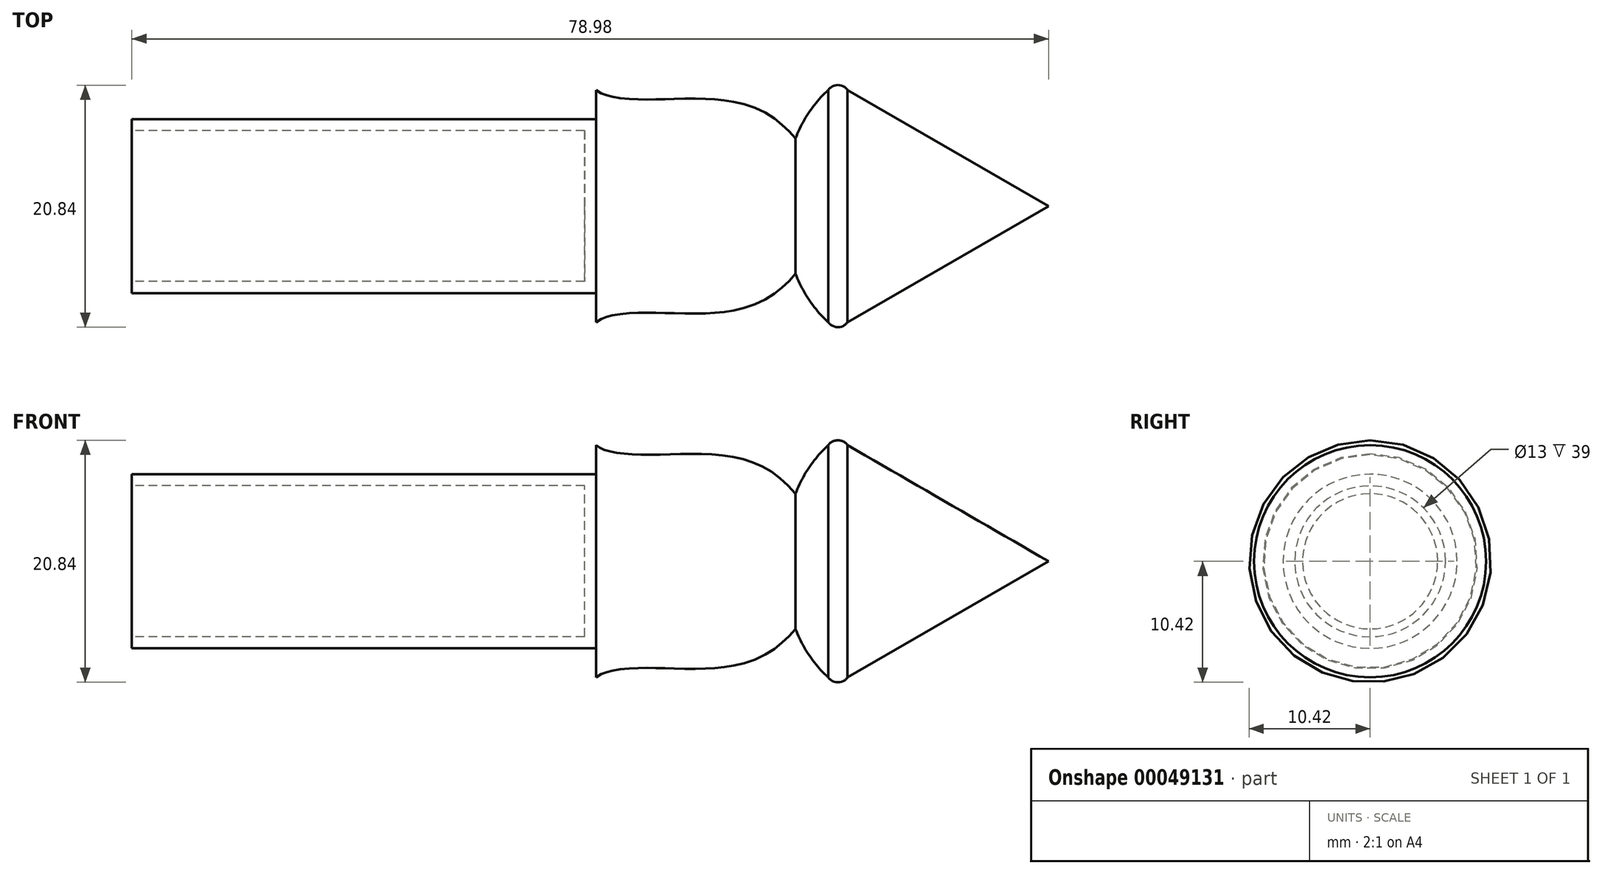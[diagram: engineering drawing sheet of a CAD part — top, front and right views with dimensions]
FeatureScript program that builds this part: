
annotation { "Feature Type Name" : "Feature", "Feature Type Description" : "" }
export const myFeature = defineFeature(function(context is Context, id is Id, definition is map)
    precondition{}
    {
        {
            var Q0;
            Q0=qCreatedBy(makeId("Top.planeOp"),FACE);
            var sketch = newSketch(context, id + "F0", { "sketchPlane" : qUnion([Q0])});
            skLineSegment(sketch, "E0.bottom", {"start": v(-43.36, 7.5) * mm, "end": v(-3.36, 7.5) * mm});
            skLineSegment(sketch, "E0.top", {"start": v(-43.36, 0) * mm, "end": v(-3.36, 0) * mm});
            skLineSegment(sketch, "E0.left", {"start": v(-43.36, 7.5) * mm, "end": v(-43.36, 0) * mm});
            skLineSegment(sketch, "E0.right", {"start": v(-3.36, 7.5) * mm, "end": v(-3.36, 0) * mm});
            skLineSegment(sketch, "E1", {"start": v(-3.36, 7.5) * mm, "end": v(-3.36, 10) * mm});
            skFitSpline(sketch, "E2", {"points": [v(-3.36, 10) * mm, v(1.33, 9.18) * mm, v(11.64, 7.79) * mm, v(16.64, 0) * mm], "startDerivative": vector(7.94, -7.27) * mm, "endDerivative": vector(1.37, -16.17) * mm});
            skLineSegment(sketch, "E3", {"start": v(-3.36, 0) * mm, "end": v(16.64, 0) * mm});
            skArc(sketch, "E4", {"start": v(16.64, 10) * mm, "mid": v(14.98, 8.08) * mm, "end": v(13.82, 5.82) * mm});
            skArc(sketch, "E5", {"start": v(18.3, 10) * mm, "mid": v(17.47, 10.42) * mm, "end": v(16.64, 10) * mm});
            skLineSegment(sketch, "E6", {"start": v(18.3, 10) * mm, "end": v(35.62, 0) * mm});
            skLineSegment(sketch, "E7", {"start": v(35.62, 0) * mm, "end": v(16.64, 0) * mm});
            skSolve(sketch);
        }
        {
            var Q0;
            Q0=makeQuery(id+"F0.imprint","IMPRINT",FACE,{"disambiguationData":[TD([[makeQuery(id+"F0.imprint","IMPRINT",EDGE,{"derivedFrom":sQuery(id+"F0.wireOp",EDGE,"E0.bottom")}),-1.0]])]});
            var Q1;
            Q1=sQuery(id+"F0.wireOp",EDGE,"E0.top");
            revolve(context, id + "F1", {"entities" : qUnion([Q0]), "axis" : qUnion([Q1]), "revolveType" : RevolveType.FULL});
        }
        {
            var Q0;
            Q0=makeQuery(id+"F1.opRevolve","SWEPT_FACE",FACE,{"disambiguationData":[OSD([sQuery(id+"F0.wireOp",EDGE,"E0.left")])]});
            shell(context, id + "F2", {"entities" : qUnion([Q0]), "thickness" : 1 * mm});
        }
        {
            var Q0;
            Q0=makeQuery(id+"F0.imprint","IMPRINT",FACE,{"disambiguationData":[TD([[makeQuery(id+"F0.imprint","IMPRINT",EDGE,{"derivedFrom":sQuery(id+"F0.wireOp",EDGE,"E0.right")}),1.0]])]});
            var Q1;
            {var subQ2=sQuery(id+"F0.wireOp",EDGE,"E4");Q1=makeQuery(id+"F0.imprint","IMPRINT",FACE,{"disambiguationData":[TD([[makeQuery(id+"F0.imprint","IMPRINT",EDGE,{"derivedFrom":subQ2}),1.0]])]});}
            var Q2;
            Q2=sQuery(id+"F0.wireOp",EDGE,"E3");
            revolve(context, id + "F3", {"operationType" : NewBodyOperationType.ADD, "entities" : qUnion([Q0, Q1]), "axis" : qUnion([Q2]), "revolveType" : RevolveType.FULL});
        }
    });
